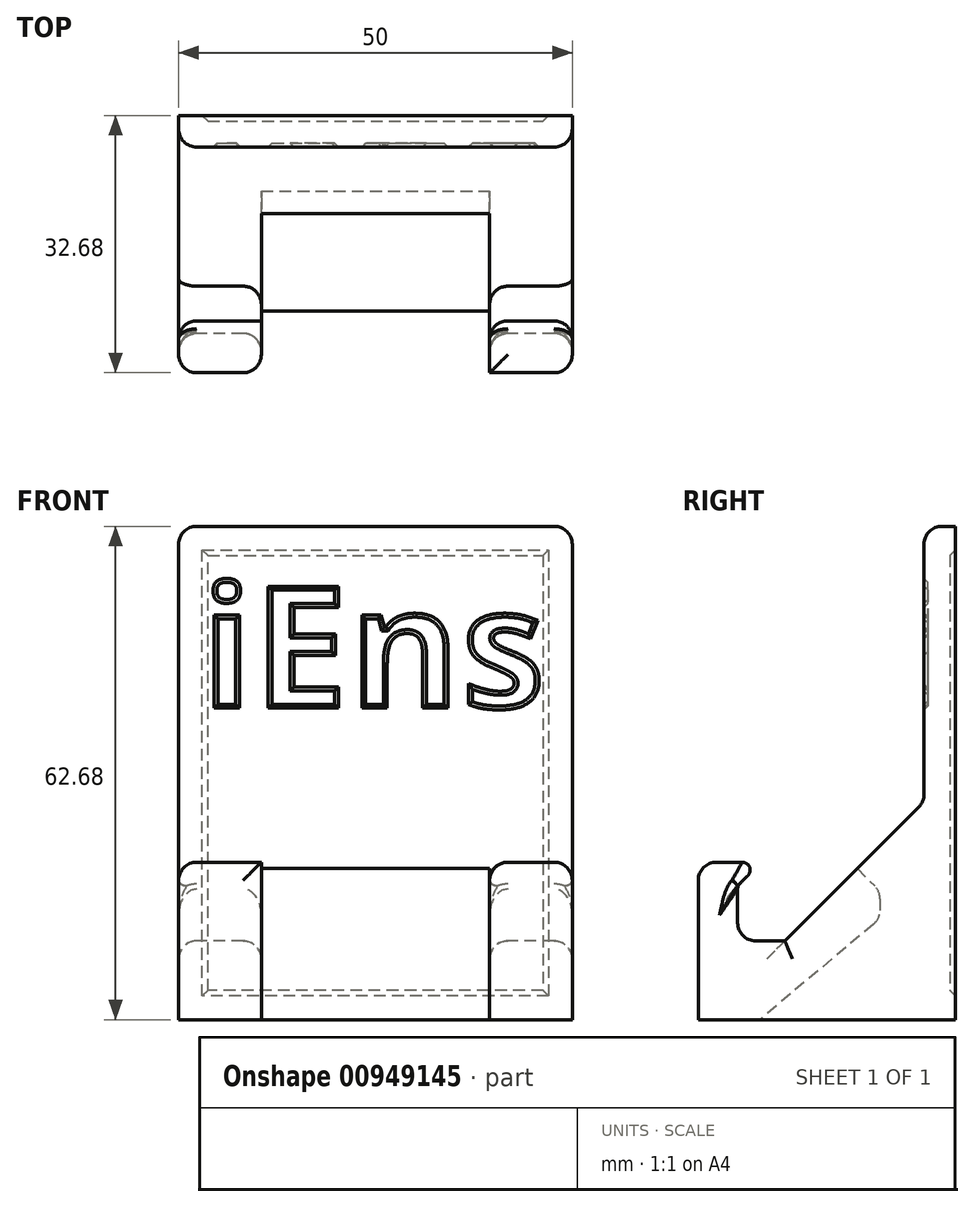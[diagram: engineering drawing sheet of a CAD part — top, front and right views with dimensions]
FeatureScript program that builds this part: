
annotation { "Feature Type Name" : "Feature", "Feature Type Description" : "" }
export const myFeature = defineFeature(function(context is Context, id is Id, definition is map)
    precondition{}
    {
        {
            var Q0;
            Q0=qCreatedBy(makeId("Right.planeOp"),FACE);
            var sketch = newSketch(context, id + "F0", { "sketchPlane" : qUnion([Q0])});
            skLineSegment(sketch, "E0.bottom", {"start": v(-28.02, 44.9) * mm, "end": v(-24.02, 44.9) * mm});
            skLineSegment(sketch, "E0.left", {"start": v(-28.02, 44.9) * mm, "end": v(-28.02, 9.9) * mm});
            skLineSegment(sketch, "E1", {"start": v(-28.02, 9.9) * mm, "end": v(-45.7, -7.78) * mm});
            skLineSegment(sketch, "E2", {"start": v(-45.7, -7.78) * mm, "end": v(-51.7, -7.78) * mm});
            skLineSegment(sketch, "E3", {"start": v(-24.02, 44.9) * mm, "end": v(-24.02, -17.78) * mm});
            skLineSegment(sketch, "E4.top", {"start": v(-51.7, 2.22) * mm, "end": v(-56.7, 2.22) * mm});
            skLineSegment(sketch, "E4.left", {"start": v(-51.7, -7.78) * mm, "end": v(-51.7, -0.78) * mm});
            skLineSegment(sketch, "E4.right", {"start": v(-56.7, -17.78) * mm, "end": v(-56.7, 2.22) * mm});
            skLineSegment(sketch, "E5", {"start": v(-56.7, -17.78) * mm, "end": v(-24.02, -17.78) * mm});
            skLineSegment(sketch, "E6", {"start": v(-51.7, 2.22) * mm, "end": v(-48.7, 2.22) * mm});
            skLineSegment(sketch, "E7", {"start": v(-48.7, 2.22) * mm, "end": v(-51.7, -0.78) * mm});
            skSolve(sketch);
        }
        {
            var Q0;
            Q0=makeQuery(id+"F0.imprint","IMPRINT",FACE,{"disambiguationData":[TD([[makeQuery(id+"F0.imprint","IMPRINT",EDGE,{"derivedFrom":sQuery(id+"F0.wireOp",EDGE,"E0.bottom")}),-1.0]])]});
            extrude(context, id + "F1", {"entities" : qUnion([Q0]), "depth" : 50 * mm, "offsetDistance" : 25 * mm});
        }
        {
            var Q0;
            Q0=makeQuery(id+"F1.opExtrude","CAP_FACE",FACE,{"disambiguationData":[OSD([sQuery(id+"F0.wireOp",EDGE,"E0.bottom"),sQuery(id+"F0.wireOp",EDGE,"E0.left"),sQuery(id+"F0.wireOp",EDGE,"E1"),sQuery(id+"F0.wireOp",EDGE,"E2"),sQuery(id+"F0.wireOp",EDGE,"E3"),sQuery(id+"F0.wireOp",EDGE,"E4.top"),sQuery(id+"F0.wireOp",EDGE,"E4.left"),sQuery(id+"F0.wireOp",EDGE,"E4.right"),sQuery(id+"F0.wireOp",EDGE,"E5")])],"isStart":false});
            var Q1;
            Q1=makeQuery(id+"F1.opExtrude","CAP_FACE",FACE,{"disambiguationData":[OSD([sQuery(id+"F0.wireOp",EDGE,"E0.bottom"),sQuery(id+"F0.wireOp",EDGE,"E0.left"),sQuery(id+"F0.wireOp",EDGE,"E1"),sQuery(id+"F0.wireOp",EDGE,"E2"),sQuery(id+"F0.wireOp",EDGE,"E3"),sQuery(id+"F0.wireOp",EDGE,"E4.top"),sQuery(id+"F0.wireOp",EDGE,"E4.left"),sQuery(id+"F0.wireOp",EDGE,"E4.right"),sQuery(id+"F0.wireOp",EDGE,"E5")])],"isStart":true});
            cPlane(context, id + "F2", {"entities" : qUnion([Q0, Q1]), "cplaneType" : CPlaneType.MID_PLANE, "offset" : 20 * mm, "width" : 150 * mm, "height" : 150 * mm});
        }
        {
            var Q0;
            Q0=qCreatedBy(id+"F2.planeOp",FACE);
            var sketch = newSketch(context, id + "F3", { "sketchPlane" : qUnion([Q0])});
            skLineSegment(sketch, "E8", {"start": v(-36.5, 1.42) * mm, "end": v(-33.62, -1.48) * mm});
            skLineSegment(sketch, "E9", {"start": v(-33.62, -1.48) * mm, "end": v(-33.62, -4.96) * mm});
            skLineSegment(sketch, "E10", {"start": v(-33.62, -4.96) * mm, "end": v(-48.9, -17.78) * mm});
            skLineSegment(sketch, "E11", {"start": v(-48.9, -17.78) * mm, "end": v(-56.7, -17.78) * mm});
            skLineSegment(sketch, "E12", {"start": v(-56.7, -17.78) * mm, "end": v(-56.7, 2.22) * mm});
            skLineSegment(sketch, "E13", {"start": v(-45.7, -7.78) * mm, "end": v(-36.5, 1.42) * mm});
            skLineSegment(sketch, "E14", {"start": v(-45.7, -7.78) * mm, "end": v(-45.7, 2.22) * mm});
            skLineSegment(sketch, "E15", {"start": v(-45.7, 2.22) * mm, "end": v(-56.7, 2.22) * mm});
            skSolve(sketch);
        }
        {
            var Q0;
            Q0=makeQuery(id+"F3.imprint","IMPRINT",FACE,{"disambiguationData":[TD([[makeQuery(id+"F3.imprint","IMPRINT",EDGE,{"derivedFrom":sQuery(id+"F3.wireOp",EDGE,"E8")}),-1.0]])]});
            extrude(context, id + "F4", {"entities" : qUnion([Q0]), "operationType" : NewBodyOperationType.REMOVE, "endBound" : BoundingType.SYMMETRIC, "oppositeDirection" : true, "depth" : 29 * mm, "offsetDistance" : 25 * mm});
        }
        {
            var Q0;
            Q0=makeQuery(id+"F1.opExtrude","SWEPT_FACE",FACE,{"disambiguationData":[OSD([sQuery(id+"F0.wireOp",EDGE,"E3")])]});
            var sketch = newSketch(context, id + "F5", { "sketchPlane" : qUnion([Q0])});
            skLineSegment(sketch, "E16.bottom", {"start": v(-47, 41.9) * mm, "end": v(-3, 41.9) * mm});
            skLineSegment(sketch, "E16.top", {"start": v(-47, -14.78) * mm, "end": v(-3, -14.78) * mm});
            skLineSegment(sketch, "E16.left", {"start": v(-47, 41.9) * mm, "end": v(-47, -14.78) * mm});
            skLineSegment(sketch, "E16.right", {"start": v(-3, 41.9) * mm, "end": v(-3, -14.78) * mm});
            skSolve(sketch);
        }
        {
            var Q0;
            Q0=makeQuery(id+"F5.imprint","IMPRINT",FACE,{"disambiguationData":[TD([[makeQuery(id+"F5.imprint","IMPRINT",EDGE,{"derivedFrom":sQuery(id+"F5.wireOp",EDGE,"E16.bottom")}),-1.0]])]});
            extrude(context, id + "F6", {"entities" : qUnion([Q0]), "operationType" : NewBodyOperationType.REMOVE, "flatOperationType" : FlatOperationType.REMOVE, "oppositeDirection" : true, "depth" : 0.7 * mm, "offsetDistance" : 25 * mm, "hasDraft" : true, "draftAngle" : 45 * degree, "draftPullDirection" : true, "domain" : OperationDomain.MODEL});
        }
        {
            var Q0;
            Q0=makeQuery(id+"F1.opExtrude","SWEPT_EDGE",EDGE,{"disambiguationData":[OSD([sQuery(id+"F0.wireOp",EDGE,"E0.bottom"),sQuery(id+"F0.wireOp",EDGE,"E0.left")])]});
            var Q1;
            Q1=makeQuery(id+"F1.opExtrude","CAP_EDGE",EDGE,{"disambiguationData":[OSD([sQuery(id+"F0.wireOp",EDGE,"E0.left")])],"isStart":false});
            var Q2;
            Q2=makeQuery(id+"F1.opExtrude","CAP_EDGE",EDGE,{"disambiguationData":[OSD([sQuery(id+"F0.wireOp",EDGE,"E1")])],"isStart":false});
            var Q3;
            Q3=makeQuery(id+"F1.opExtrude","CAP_EDGE",EDGE,{"disambiguationData":[OSD([sQuery(id+"F0.wireOp",EDGE,"E2")])],"isStart":false});
            var Q4;
            Q4=makeQuery(id+"F1.opExtrude","CAP_EDGE",EDGE,{"disambiguationData":[OSD([sQuery(id+"F0.wireOp",EDGE,"E0.left")])],"isStart":true});
            var Q5;
            Q5=makeQuery(id+"F1.opExtrude","CAP_EDGE",EDGE,{"disambiguationData":[OSD([sQuery(id+"F0.wireOp",EDGE,"E1")])],"isStart":true});
            var Q6;
            Q6=makeQuery(id+"F1.opExtrude","SWEPT_EDGE",EDGE,{"disambiguationData":[OSD([sQuery(id+"F0.wireOp",EDGE,"E0.left"),sQuery(id+"F0.wireOp",EDGE,"E1")])]});
            var Q7;
            Q7=makeQuery(id+"F1.opExtrude","CAP_EDGE",EDGE,{"disambiguationData":[OSD([sQuery(id+"F0.wireOp",EDGE,"E2")])],"isStart":true});
            var Q8;
            Q8=makeQuery(id+"F1.opExtrude","CAP_EDGE",EDGE,{"disambiguationData":[OSD([sQuery(id+"F0.wireOp",EDGE,"E4.left")])],"isStart":true});
            var Q9;
            Q9=makeQuery(id+"F4.boolean.opBoolean","INTERSECT",EDGE,{"derivedFrom":[makeQuery(id+"F1.opExtrude","SWEPT_FACE",FACE,{"disambiguationData":[OSD([sQuery(id+"F0.wireOp",EDGE,"E4.left")])]}),makeQuery(id+"F4.opExtrude","CAP_FACE",FACE,{"disambiguationData":[OSD([sQuery(id+"F3.wireOp",EDGE,"E8"),sQuery(id+"F3.wireOp",EDGE,"E9"),sQuery(id+"F3.wireOp",EDGE,"E10"),sQuery(id+"F3.wireOp",EDGE,"E11"),sQuery(id+"F3.wireOp",EDGE,"E12"),sQuery(id+"F3.wireOp",EDGE,"E13"),sQuery(id+"F3.wireOp",EDGE,"E14"),sQuery(id+"F3.wireOp",EDGE,"E15")])],"isStart":false})]});
            var Q10;
            Q10=makeQuery(id+"F4.boolean.opBoolean","INTERSECT",EDGE,{"derivedFrom":[makeQuery(id+"F1.opExtrude","SWEPT_FACE",FACE,{"disambiguationData":[OSD([sQuery(id+"F0.wireOp",EDGE,"E2")])]}),makeQuery(id+"F4.opExtrude","CAP_FACE",FACE,{"disambiguationData":[OSD([sQuery(id+"F3.wireOp",EDGE,"E8"),sQuery(id+"F3.wireOp",EDGE,"E9"),sQuery(id+"F3.wireOp",EDGE,"E10"),sQuery(id+"F3.wireOp",EDGE,"E11"),sQuery(id+"F3.wireOp",EDGE,"E12"),sQuery(id+"F3.wireOp",EDGE,"E13"),sQuery(id+"F3.wireOp",EDGE,"E14"),sQuery(id+"F3.wireOp",EDGE,"E15")])],"isStart":false})]});
            var Q11;
            Q11=makeQuery(id+"F4.boolean.opBoolean","COPY",EDGE,{"derivedFrom":makeQuery(id+"F4.opExtrude","CAP_EDGE",EDGE,{"disambiguationData":[OSD([sQuery(id+"F3.wireOp",EDGE,"E13")])],"isStart":false})});
            var Q12;
            Q12=makeQuery(id+"F4.boolean.opBoolean","COPY",EDGE,{"derivedFrom":makeQuery(id+"F4.opExtrude","SWEPT_EDGE",EDGE,{"disambiguationData":[OSD([sQuery(id+"F3.wireOp",EDGE,"E8"),sQuery(id+"F3.wireOp",EDGE,"E13")])]})});
            var Q13;
            Q13=makeQuery(id+"F4.boolean.opBoolean","COPY",EDGE,{"derivedFrom":makeQuery(id+"F4.opExtrude","CAP_EDGE",EDGE,{"disambiguationData":[OSD([sQuery(id+"F3.wireOp",EDGE,"E13")])],"isStart":true})});
            var Q14;
            Q14=makeQuery(id+"F4.boolean.opBoolean","INTERSECT",EDGE,{"derivedFrom":[makeQuery(id+"F1.opExtrude","SWEPT_FACE",FACE,{"disambiguationData":[OSD([sQuery(id+"F0.wireOp",EDGE,"E2")])]}),makeQuery(id+"F4.opExtrude","CAP_FACE",FACE,{"disambiguationData":[OSD([sQuery(id+"F3.wireOp",EDGE,"E8"),sQuery(id+"F3.wireOp",EDGE,"E9"),sQuery(id+"F3.wireOp",EDGE,"E10"),sQuery(id+"F3.wireOp",EDGE,"E11"),sQuery(id+"F3.wireOp",EDGE,"E12"),sQuery(id+"F3.wireOp",EDGE,"E13"),sQuery(id+"F3.wireOp",EDGE,"E14"),sQuery(id+"F3.wireOp",EDGE,"E15")])],"isStart":true})]});
            var Q15;
            Q15=makeQuery(id+"F4.boolean.opBoolean","INTERSECT",EDGE,{"derivedFrom":[makeQuery(id+"F1.opExtrude","SWEPT_FACE",FACE,{"disambiguationData":[OSD([sQuery(id+"F0.wireOp",EDGE,"E4.left")])]}),makeQuery(id+"F4.opExtrude","CAP_FACE",FACE,{"disambiguationData":[OSD([sQuery(id+"F3.wireOp",EDGE,"E8"),sQuery(id+"F3.wireOp",EDGE,"E9"),sQuery(id+"F3.wireOp",EDGE,"E10"),sQuery(id+"F3.wireOp",EDGE,"E11"),sQuery(id+"F3.wireOp",EDGE,"E12"),sQuery(id+"F3.wireOp",EDGE,"E13"),sQuery(id+"F3.wireOp",EDGE,"E14"),sQuery(id+"F3.wireOp",EDGE,"E15")])],"isStart":true})]});
            var Q16;
            Q16=makeQuery(id+"F1.opExtrude","CAP_EDGE",EDGE,{"disambiguationData":[OSD([sQuery(id+"F0.wireOp",EDGE,"E4.left")])],"isStart":false});
            var Q17;
            {var subQ0=sQuery(id+"F0.wireOp",EDGE,"E4.right");var subQ1=sQuery(id+"F0.wireOp",EDGE,"E4.top");Q17=makeQuery(id+"F4.boolean.opBoolean","SPLIT",EDGE,{"disambiguationData":[TD([makeQuery(id+"F4.opExtrude","CAP_FACE",FACE,{"disambiguationData":[OSD([sQuery(id+"F3.wireOp",EDGE,"E8"),sQuery(id+"F3.wireOp",EDGE,"E9"),sQuery(id+"F3.wireOp",EDGE,"E10"),sQuery(id+"F3.wireOp",EDGE,"E11"),sQuery(id+"F3.wireOp",EDGE,"E12"),sQuery(id+"F3.wireOp",EDGE,"E13"),sQuery(id+"F3.wireOp",EDGE,"E14"),sQuery(id+"F3.wireOp",EDGE,"E15")])],"isStart":false})])],"derivedFrom":makeQuery(id+"F1.opExtrude","SWEPT_EDGE",EDGE,{"disambiguationData":[OSD([subQ1,subQ0])]})});}
            var Q18;
            Q18=makeQuery(id+"F4.boolean.opBoolean","COPY",EDGE,{"derivedFrom":makeQuery(id+"F4.opExtrude","CAP_EDGE",EDGE,{"disambiguationData":[OSD([sQuery(id+"F3.wireOp",EDGE,"E12")])],"isStart":false})});
            var Q19;
            Q19=makeQuery(id+"F1.opExtrude","CAP_EDGE",EDGE,{"disambiguationData":[OSD([sQuery(id+"F0.wireOp",EDGE,"E4.right")])],"isStart":true});
            var Q20;
            Q20=makeQuery(id+"F4.boolean.opBoolean","COPY",EDGE,{"derivedFrom":makeQuery(id+"F4.opExtrude","CAP_EDGE",EDGE,{"disambiguationData":[OSD([sQuery(id+"F3.wireOp",EDGE,"E12")])],"isStart":true})});
            var Q21;
            {var subQ0=sQuery(id+"F0.wireOp",EDGE,"E4.right");var subQ1=sQuery(id+"F0.wireOp",EDGE,"E4.top");Q21=makeQuery(id+"F4.boolean.opBoolean","SPLIT",EDGE,{"disambiguationData":[TD([makeQuery(id+"F4.opExtrude","CAP_FACE",FACE,{"disambiguationData":[OSD([sQuery(id+"F3.wireOp",EDGE,"E8"),sQuery(id+"F3.wireOp",EDGE,"E9"),sQuery(id+"F3.wireOp",EDGE,"E10"),sQuery(id+"F3.wireOp",EDGE,"E11"),sQuery(id+"F3.wireOp",EDGE,"E12"),sQuery(id+"F3.wireOp",EDGE,"E13"),sQuery(id+"F3.wireOp",EDGE,"E14"),sQuery(id+"F3.wireOp",EDGE,"E15")])],"isStart":true})])],"derivedFrom":makeQuery(id+"F1.opExtrude","SWEPT_EDGE",EDGE,{"disambiguationData":[OSD([subQ1,subQ0])]})});}
            var Q22;
            Q22=makeQuery(id+"F1.opExtrude","CAP_EDGE",EDGE,{"disambiguationData":[OSD([sQuery(id+"F0.wireOp",EDGE,"E4.right")])],"isStart":false});
            var Q23;
            Q23=makeQuery(id+"F4.boolean.opBoolean","COPY",EDGE,{"derivedFrom":makeQuery(id+"F4.opExtrude","SWEPT_EDGE",EDGE,{"disambiguationData":[OSD([sQuery(id+"F3.wireOp",EDGE,"E10"),sQuery(id+"F3.wireOp",EDGE,"E11")])]})});
            var Q24;
            Q24=makeQuery(id+"F4.boolean.opBoolean","COPY",EDGE,{"derivedFrom":makeQuery(id+"F4.opExtrude","SWEPT_EDGE",EDGE,{"disambiguationData":[OSD([sQuery(id+"F3.wireOp",EDGE,"E9"),sQuery(id+"F3.wireOp",EDGE,"E10")])]})});
            var Q25;
            Q25=makeQuery(id+"F4.boolean.opBoolean","COPY",EDGE,{"derivedFrom":makeQuery(id+"F4.opExtrude","SWEPT_EDGE",EDGE,{"disambiguationData":[OSD([sQuery(id+"F3.wireOp",EDGE,"E8"),sQuery(id+"F3.wireOp",EDGE,"E9")])]})});
            var Q26;
            Q26=makeQuery(id+"F1.opExtrude","CAP_EDGE",EDGE,{"disambiguationData":[OSD([sQuery(id+"F0.wireOp",EDGE,"E4.top")])],"isStart":false});
            var Q27;
            Q27=makeQuery(id+"F4.boolean.opBoolean","COPY",EDGE,{"derivedFrom":makeQuery(id+"F4.opExtrude","CAP_EDGE",EDGE,{"disambiguationData":[OSD([sQuery(id+"F3.wireOp",EDGE,"E15")])],"isStart":true})});
            var Q28;
            Q28=makeQuery(id+"F4.boolean.opBoolean","COPY",EDGE,{"derivedFrom":makeQuery(id+"F4.opExtrude","CAP_EDGE",EDGE,{"disambiguationData":[OSD([sQuery(id+"F3.wireOp",EDGE,"E15")])],"isStart":false})});
            var Q29;
            Q29=makeQuery(id+"F1.opExtrude","CAP_EDGE",EDGE,{"disambiguationData":[OSD([sQuery(id+"F0.wireOp",EDGE,"E4.top")])],"isStart":true});
            var Q30;
            Q30=makeQuery(id+"F1.opExtrude","CAP_EDGE",EDGE,{"disambiguationData":[OSD([sQuery(id+"F0.wireOp",EDGE,"E0.bottom")])],"isStart":false});
            var Q31;
            Q31=makeQuery(id+"F1.opExtrude","CAP_EDGE",EDGE,{"disambiguationData":[OSD([sQuery(id+"F0.wireOp",EDGE,"E0.bottom")])],"isStart":true});
            var Q32;
            {var subQ1=sQuery(id+"F0.wireOp",EDGE,"E4.right");var subQ2=sQuery(id+"F0.wireOp",EDGE,"E4.top");Q32=makeQuery(id+"F4.boolean.opBoolean","SPLIT",EDGE,{"disambiguationData":[TD([makeQuery(id+"F4.opExtrude","CAP_FACE",FACE,{"disambiguationData":[OSD([sQuery(id+"F3.wireOp",EDGE,"E8"),sQuery(id+"F3.wireOp",EDGE,"E9"),sQuery(id+"F3.wireOp",EDGE,"E10"),sQuery(id+"F3.wireOp",EDGE,"E11"),sQuery(id+"F3.wireOp",EDGE,"E12"),sQuery(id+"F3.wireOp",EDGE,"E13"),sQuery(id+"F3.wireOp",EDGE,"E14"),sQuery(id+"F3.wireOp",EDGE,"E15")])],"isStart":true})])],"derivedFrom":makeQuery(id+"F1.opExtrude","SWEPT_EDGE",EDGE,{"disambiguationData":[OSD([subQ2,subQ1])]})});}
            var Q33;
            {var subQ0=sQuery(id+"F0.wireOp",EDGE,"E4.left");var subQ1=sQuery(id+"F0.wireOp",EDGE,"E2");Q33=makeQuery(id+"F4.boolean.opBoolean","SPLIT",EDGE,{"disambiguationData":[TD([makeQuery(id+"F4.opExtrude","CAP_FACE",FACE,{"disambiguationData":[OSD([sQuery(id+"F3.wireOp",EDGE,"E8"),sQuery(id+"F3.wireOp",EDGE,"E9"),sQuery(id+"F3.wireOp",EDGE,"E10"),sQuery(id+"F3.wireOp",EDGE,"E11"),sQuery(id+"F3.wireOp",EDGE,"E12"),sQuery(id+"F3.wireOp",EDGE,"E13"),sQuery(id+"F3.wireOp",EDGE,"E14"),sQuery(id+"F3.wireOp",EDGE,"E15")])],"isStart":true})])],"derivedFrom":makeQuery(id+"F1.opExtrude","SWEPT_EDGE",EDGE,{"disambiguationData":[OSD([subQ1,subQ0])]})});}
            var Q34;
            {var subQ0=sQuery(id+"F0.wireOp",EDGE,"E4.left");var subQ1=sQuery(id+"F0.wireOp",EDGE,"E2");Q34=makeQuery(id+"F4.boolean.opBoolean","SPLIT",EDGE,{"disambiguationData":[TD([makeQuery(id+"F4.opExtrude","CAP_FACE",FACE,{"disambiguationData":[OSD([sQuery(id+"F3.wireOp",EDGE,"E8"),sQuery(id+"F3.wireOp",EDGE,"E9"),sQuery(id+"F3.wireOp",EDGE,"E10"),sQuery(id+"F3.wireOp",EDGE,"E11"),sQuery(id+"F3.wireOp",EDGE,"E12"),sQuery(id+"F3.wireOp",EDGE,"E13"),sQuery(id+"F3.wireOp",EDGE,"E14"),sQuery(id+"F3.wireOp",EDGE,"E15")])],"isStart":false})])],"derivedFrom":makeQuery(id+"F1.opExtrude","SWEPT_EDGE",EDGE,{"disambiguationData":[OSD([subQ1,subQ0])]})});}
            var Q35;
            {var subQ1=sQuery(id+"F0.wireOp",EDGE,"E4.right");var subQ2=sQuery(id+"F0.wireOp",EDGE,"E4.top");Q35=makeQuery(id+"F4.boolean.opBoolean","SPLIT",EDGE,{"disambiguationData":[TD([makeQuery(id+"F4.opExtrude","CAP_FACE",FACE,{"disambiguationData":[OSD([sQuery(id+"F3.wireOp",EDGE,"E8"),sQuery(id+"F3.wireOp",EDGE,"E9"),sQuery(id+"F3.wireOp",EDGE,"E10"),sQuery(id+"F3.wireOp",EDGE,"E11"),sQuery(id+"F3.wireOp",EDGE,"E12"),sQuery(id+"F3.wireOp",EDGE,"E13"),sQuery(id+"F3.wireOp",EDGE,"E14"),sQuery(id+"F3.wireOp",EDGE,"E15")])],"isStart":false})])],"derivedFrom":makeQuery(id+"F1.opExtrude","SWEPT_EDGE",EDGE,{"disambiguationData":[OSD([subQ2,subQ1])]})});}
            fillet(context, id + "F7", {"entities" : qUnion([Q0, Q1, Q2, Q3, Q4, Q5, Q6, Q7, Q8, Q9, Q10, Q11, Q12, Q13, Q14, Q15, Q16, Q17, Q18, Q19, Q20, Q21, Q22, Q23, Q24, Q25, Q26, Q27, Q28, Q29, Q30, Q31, Q32, Q33, Q34, Q35]), "radius" : 2.3 * mm, "tangentPropagation" : true, "allowEdgeOverflow" : false});
        }
        {
            var Q0;
            Q0=makeQuery(id+"F1.opExtrude","SWEPT_FACE",FACE,{"disambiguationData":[OSD([sQuery(id+"F0.wireOp",EDGE,"E0.left")])]});
            var sketch = newSketch(context, id + "F8", { "sketchPlane" : qUnion([Q0])});
            skText(sketch, "E17", { "text": "iEns", "fontName": "OpenSans-Bold.ttf"});
            skPoint(sketch, "E18", {"position": v(25, 42.6) * mm});
            skPoint(sketch, "E19", {"position": v(25, 29.6) * mm});
            skLineSegment(sketch, "E20", {"start": v(25, 42.6) * mm, "end": v(25, 10.85) * mm, "construction": true});
            const initialGuessF8  = {"E17": [0.0028, 0.02179, 1, 0, 0.01562]};
            skSetInitialGuess(sketch, initialGuessF8);
            skSolve(sketch);
        }
        {
            var Q0;
            Q0=makeQuery(id+"F8.imprint","IMPRINT",FACE,{"disambiguationData":[TD([[makeQuery(id+"F8.imprint","IMPRINT",EDGE,{"derivedFrom":sQuery(id+"F8.wireOp",EDGE,"E17.sketch_text.stroke-5")}),-1.0]])]});
            var Q1;
            Q1=makeQuery(id+"F8.imprint","IMPRINT",FACE,{"disambiguationData":[TD([[makeQuery(id+"F8.imprint","IMPRINT",EDGE,{"derivedFrom":sQuery(id+"F8.wireOp",EDGE,"E17.sketch_text.stroke-0")}),-1.0]])]});
            var Q2;
            Q2=makeQuery(id+"F8.imprint","IMPRINT",FACE,{"disambiguationData":[TD([[makeQuery(id+"F8.imprint","IMPRINT",EDGE,{"derivedFrom":sQuery(id+"F8.wireOp",EDGE,"E17.sketch_text.stroke-9")}),-1.0]])]});
            var Q3;
            Q3=makeQuery(id+"F8.imprint","IMPRINT",FACE,{"disambiguationData":[TD([[makeQuery(id+"F8.imprint","IMPRINT",EDGE,{"derivedFrom":sQuery(id+"F8.wireOp",EDGE,"E17.sketch_text.stroke-21")}),-1.0]])]});
            var Q4;
            Q4=makeQuery(id+"F8.imprint","IMPRINT",FACE,{"disambiguationData":[TD([[makeQuery(id+"F8.imprint","IMPRINT",EDGE,{"derivedFrom":sQuery(id+"F8.wireOp",EDGE,"E17.sketch_text.stroke-38")}),-1.0]])]});
            extrude(context, id + "F9", {"entities" : qUnion([Q0, Q1, Q2, Q3, Q4]), "operationType" : NewBodyOperationType.REMOVE, "oppositeDirection" : true, "depth" : .5 * mm, "offsetDistance" : 25 * mm, "hasDraft" : true, "draftAngle" : 45 * degree, "draftPullDirection" : true});
        }
        {
            var Q0;
            {var subQ0=sQuery(id+"F0.wireOp",EDGE,"E7");var subQ1=sQuery(id+"F0.wireOp",EDGE,"E6");Q0=makeQuery(id+"F4.boolean.opBoolean","SPLIT",EDGE,{"disambiguationData":[TD([makeQuery(id+"F4.opExtrude","CAP_FACE",FACE,{"disambiguationData":[OSD([sQuery(id+"F3.wireOp",EDGE,"E8"),sQuery(id+"F3.wireOp",EDGE,"E9"),sQuery(id+"F3.wireOp",EDGE,"E10"),sQuery(id+"F3.wireOp",EDGE,"E11"),sQuery(id+"F3.wireOp",EDGE,"E12"),sQuery(id+"F3.wireOp",EDGE,"E13"),sQuery(id+"F3.wireOp",EDGE,"E14"),sQuery(id+"F3.wireOp",EDGE,"E15")])],"isStart":true})])],"derivedFrom":makeQuery(id+"F1.opExtrude","SWEPT_EDGE",EDGE,{"disambiguationData":[OSD([subQ1,subQ0])]})});}
            var Q1;
            {var subQ0=sQuery(id+"F0.wireOp",EDGE,"E7");var subQ1=sQuery(id+"F0.wireOp",EDGE,"E6");Q1=makeQuery(id+"F4.boolean.opBoolean","SPLIT",EDGE,{"disambiguationData":[TD([makeQuery(id+"F4.opExtrude","CAP_FACE",FACE,{"disambiguationData":[OSD([sQuery(id+"F3.wireOp",EDGE,"E8"),sQuery(id+"F3.wireOp",EDGE,"E9"),sQuery(id+"F3.wireOp",EDGE,"E10"),sQuery(id+"F3.wireOp",EDGE,"E11"),sQuery(id+"F3.wireOp",EDGE,"E12"),sQuery(id+"F3.wireOp",EDGE,"E13"),sQuery(id+"F3.wireOp",EDGE,"E14"),sQuery(id+"F3.wireOp",EDGE,"E15")])],"isStart":false})])],"derivedFrom":makeQuery(id+"F1.opExtrude","SWEPT_EDGE",EDGE,{"disambiguationData":[OSD([subQ1,subQ0])]})});}
            var Q2;
            {var subQ0=sQuery(id+"F0.wireOp",EDGE,"E7");var subQ1=sQuery(id+"F0.wireOp",EDGE,"E4.left");Q2=makeQuery(id+"F4.boolean.opBoolean","SPLIT",EDGE,{"disambiguationData":[TD([makeQuery(id+"F4.opExtrude","CAP_FACE",FACE,{"disambiguationData":[OSD([sQuery(id+"F3.wireOp",EDGE,"E8"),sQuery(id+"F3.wireOp",EDGE,"E9"),sQuery(id+"F3.wireOp",EDGE,"E10"),sQuery(id+"F3.wireOp",EDGE,"E11"),sQuery(id+"F3.wireOp",EDGE,"E12"),sQuery(id+"F3.wireOp",EDGE,"E13"),sQuery(id+"F3.wireOp",EDGE,"E14"),sQuery(id+"F3.wireOp",EDGE,"E15")])],"isStart":true})])],"derivedFrom":makeQuery(id+"F1.opExtrude","SWEPT_EDGE",EDGE,{"disambiguationData":[OSD([subQ1,subQ0])]})});}
            var Q3;
            {var subQ0=sQuery(id+"F0.wireOp",EDGE,"E7");var subQ1=sQuery(id+"F0.wireOp",EDGE,"E4.left");Q3=makeQuery(id+"F4.boolean.opBoolean","SPLIT",EDGE,{"disambiguationData":[TD([makeQuery(id+"F4.opExtrude","CAP_FACE",FACE,{"disambiguationData":[OSD([sQuery(id+"F3.wireOp",EDGE,"E8"),sQuery(id+"F3.wireOp",EDGE,"E9"),sQuery(id+"F3.wireOp",EDGE,"E10"),sQuery(id+"F3.wireOp",EDGE,"E11"),sQuery(id+"F3.wireOp",EDGE,"E12"),sQuery(id+"F3.wireOp",EDGE,"E13"),sQuery(id+"F3.wireOp",EDGE,"E14"),sQuery(id+"F3.wireOp",EDGE,"E15")])],"isStart":false})])],"derivedFrom":makeQuery(id+"F1.opExtrude","SWEPT_EDGE",EDGE,{"disambiguationData":[OSD([subQ1,subQ0])]})});}
            fillet(context, id + "F10", {"entities" : qUnion([Q0, Q1, Q2, Q3]), "radius" : 1 * mm, "tangentPropagation" : true, "allowEdgeOverflow" : false});
        }
    });
